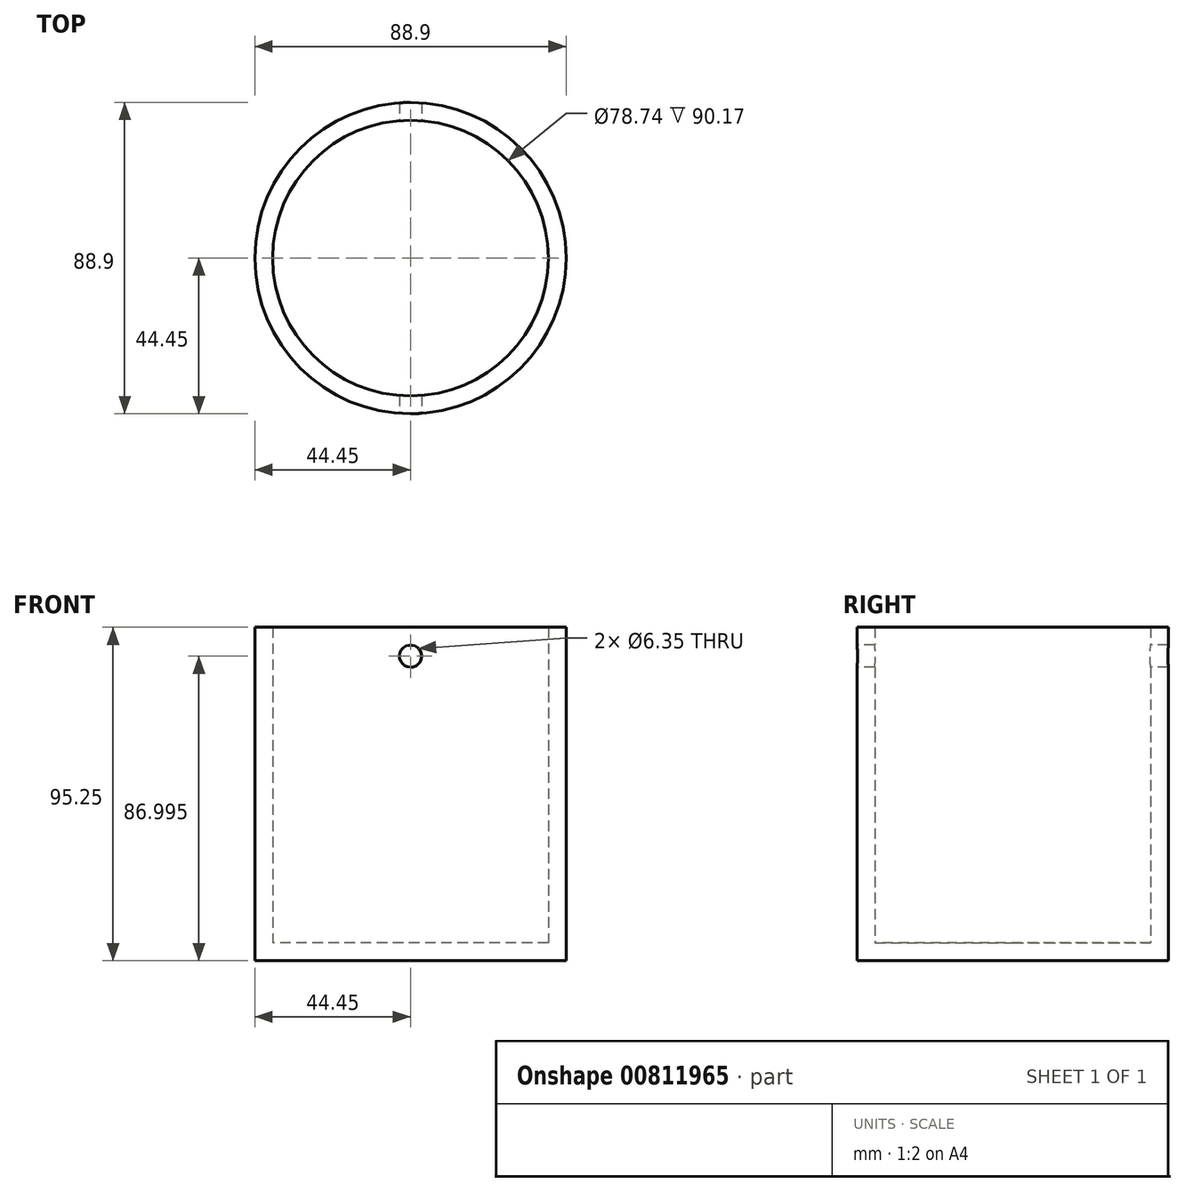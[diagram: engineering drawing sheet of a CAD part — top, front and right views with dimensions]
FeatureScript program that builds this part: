
annotation { "Feature Type Name" : "Feature", "Feature Type Description" : "" }
export const myFeature = defineFeature(function(context is Context, id is Id, definition is map)
    precondition{}
    {
        {
            var Q0;
            Q0=qCreatedBy(makeId("Top.planeOp"),FACE);
            var sketch = newSketch(context, id + "F0", { "sketchPlane" : qUnion([Q0])});
            skCircle(sketch, "E0", {"center": v(0, 0) * mm, "radius": 44.45 * mm});
            skSolve(sketch);
        }
        {
            var Q0;
            Q0 = qSketchRegion(id + "F0", true);
            extrude(context, id + "F1", {"entities" : qUnion([Q0]), "depth" : 95.25 * mm, "offsetDistance" : 25.4 * mm});
        }
        {
            var Q0;
            Q0=makeQuery(id+"F1.opExtrude","CAP_FACE",FACE,{"disambiguationData":[OSD([sQuery(id+"F0.wireOp",EDGE,"E0")])],"isStart":false});
            shell(context, id + "F2", {"entities" : qUnion([Q0]), "thickness" : 5.08 * mm});
        }
        {
            var Q0;
            Q0=qCreatedBy(makeId("Front.planeOp"),FACE);
            var sketch = newSketch(context, id + "F3", { "sketchPlane" : qUnion([Q0])});
            skCircle(sketch, "E1", {"center": v(0, 87) * mm, "radius": 3.18 * mm});
            skSolve(sketch);
        }
        {
            var Q0;
            Q0 = qSketchRegion(id + "F3", true);
            extrude(context, id + "F4", {"entities" : qUnion([Q0]), "operationType" : NewBodyOperationType.REMOVE, "endBound" : BoundingType.THROUGH_ALL, "oppositeDirection" : true, "depth" : 25.4 * mm, "offsetDistance" : 25.4 * mm, "hasSecondDirection" : true, "secondDirectionBound" : SecondDirectionBoundingType.THROUGH_ALL, "secondDirectionOppositeDirection" : false, "secondDirectionDepth" : 25.4 * mm});
        }
    });
